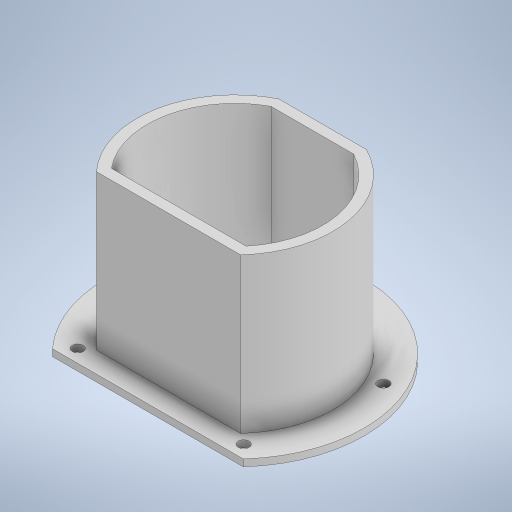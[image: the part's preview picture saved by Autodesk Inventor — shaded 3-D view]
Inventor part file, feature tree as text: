
AUTODESK INVENTOR PART (.ipt)
format: ipt  version: 2024 (Build 280153000, 153)  size: 281,600 bytes
history: native  units: mm
features: extrude x2, sketch x2, other x1, mirror x1
ambient origin geometry x8: Origin, YZ Plane, XZ Plane, XY Plane, X Axis, Y Axis, Z Axis, Center Point
bodies: Body1 (feature_tree)
feature tree (6):
  other  "ソリッド1"
  extrude  "押し出し1"  Depth=37.5733mm
  extrude  "押し出し2"  Depth=29.21mm
  mirror  "ミラー1"
  sketch  "スケッチ1"
  sketch  "スケッチ2"
